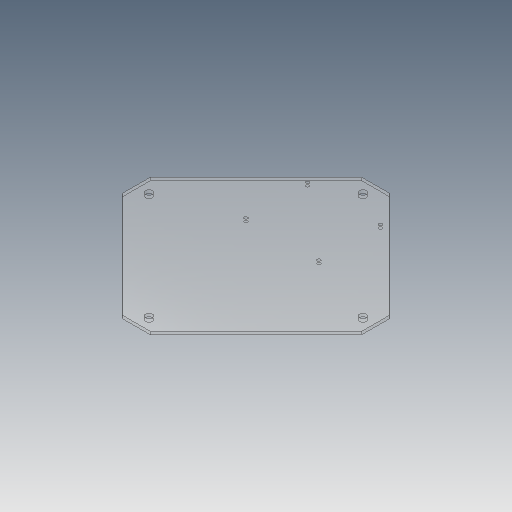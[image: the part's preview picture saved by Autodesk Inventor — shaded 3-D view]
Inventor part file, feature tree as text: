
AUTODESK INVENTOR PART (.ipt)
format: ipt  version: 2017 (Build 210142000, 142)  size: 139,264 bytes
history: native  units: mm
features: sketch x4, extrude x2, hole x2, projected_geometry x2, pattern_circular x1
ambient origin geometry x8: Origin, YZ Plane, XZ Plane, XY Plane, X Axis, Y Axis, Z Axis, Center Point
bodies: Solid1 (feature_tree)
feature tree (11):
  extrude  "Extrusion1"  Depth=40.0mm TaperAngle=360.0deg
  hole  "Hole1"  [1 undecoded]
  pattern_circular  "Circular Pattern1"  Count=15  [1 undecoded]
  extrude  "Extrusion2"  Depth=10.0mm TaperAngle=0.0deg
  hole  "Hole2"  [1 undecoded]
  sketch  "Sketch1"  dims[d7=2.38125mm d8=0.0mm]
  sketch  "Sketch2"  dims[d11=5.5mm d12=6.0mm d13=5.715mm d14=2.0mm d15=14.3117mm d16=8.0mm d17=20.594885mm d18=40.0mm d19=360.0deg]
  sketch  "Sketch3"  dims[d25=190.0mm d26=10.0mm d27=150.0mm]
  projected_geometry  "Projected Loop1"
  sketch  "Sketch4"  dims[d28=150.0mm d29=10.0mm d30=0.0mm d31=25.0mm d32=58.0mm d33=49.0mm d34=2.6mm d35=6.0mm d36=4.0mm d37=2.0mm d38=90.0deg d39=8.0mm d40=0.0mm]
  projected_geometry  "Projected Loop2"
note: 3 required parameter values undecoded (feature->parameter linkage not recoverable at this tier; creation-order binding heuristic only, values carry confidence <= 0.55)
